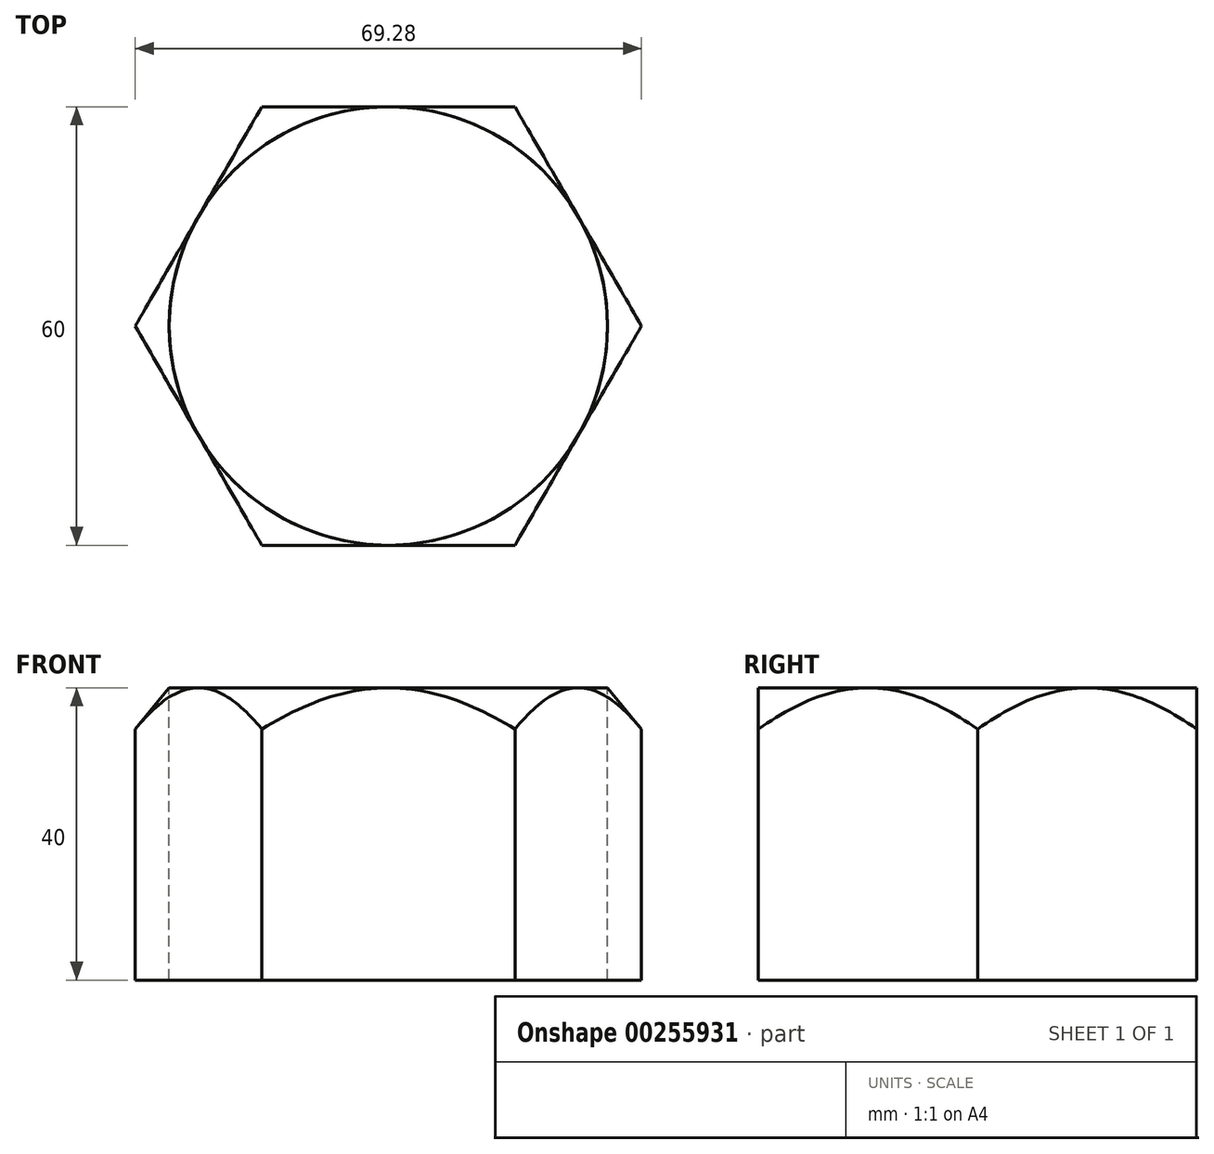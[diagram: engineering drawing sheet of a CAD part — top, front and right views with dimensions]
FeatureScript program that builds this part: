
annotation { "Feature Type Name" : "Feature", "Feature Type Description" : "" }
export const myFeature = defineFeature(function(context is Context, id is Id, definition is map)
    precondition{}
    {
        {
            var Q0;
            Q0=qCreatedBy(makeId("Top.planeOp"),FACE);
            var sketch = newSketch(context, id + "F0", { "sketchPlane" : qUnion([Q0])});
            skCircle(sketch, "E0.cCircle", {"center": v(0, 0) * mm, "radius": 30 * mm, "construction": true});
            skLineSegment(sketch, "E0.0", {"start": v(-17.32, 30) * mm, "end": v(17.32, 30) * mm});
            skLineSegment(sketch, "E0.1", {"start": v(17.32, 30) * mm, "end": v(34.64, 0) * mm});
            skLineSegment(sketch, "E0.2", {"start": v(34.64, 0) * mm, "end": v(17.32, -30) * mm});
            skLineSegment(sketch, "E0.3", {"start": v(17.32, -30) * mm, "end": v(-17.32, -30) * mm});
            skLineSegment(sketch, "E0.4", {"start": v(-17.32, -30) * mm, "end": v(-34.64, 0) * mm});
            skLineSegment(sketch, "E0.5", {"start": v(-34.64, 0) * mm, "end": v(-17.32, 30) * mm});
            skPoint(sketch, "E0.0.midPoint", {"position": v(0, 30) * mm});
            skSolve(sketch);
        }
        {
            var Q0;
            Q0=makeQuery(id+"F0.imprint","IMPRINT",FACE,{"disambiguationData":[TD([[makeQuery(id+"F0.imprint","IMPRINT",EDGE,{"derivedFrom":sQuery(id+"F0.wireOp",EDGE,"E0.0")}),-1.0]])]});
            var sketch = newSketch(context, id + "F1", { "sketchPlane" : qUnion([Q0])});
            skCircle(sketch, "E1", {"center": v(0, 0) * mm, "radius": 30 * mm});
            skSolve(sketch);
        }
        {
            var Q0;
            {var subQ0=sQuery(id+"F1.wireOp",EDGE,"E1");var subQ3=makeQuery(id+"F1.imprint","INTERSECT",VERTEX,{"derivedFrom":[makeQuery(id+"F0.imprint","IMPRINT",EDGE,{"derivedFrom":sQuery(id+"F0.wireOp",EDGE,"E0.0")}),subQ0]});Q0=makeQuery(id+"F1.imprint","IMPRINT",FACE,{"disambiguationData":[TD([[makeQuery(id+"F1.imprint","IMPRINT",EDGE,{"disambiguationData":[TD([[subQ3,1.0]])],"derivedFrom":subQ0}),1.0]])]});}
            var Q1;
            Q1=makeQuery(id+"F0.imprint","IMPRINT",FACE,{"disambiguationData":[TD([[makeQuery(id+"F0.imprint","IMPRINT",EDGE,{"derivedFrom":sQuery(id+"F0.wireOp",EDGE,"E0.0")}),-1.0]])]});
            extrude(context, id + "F2", {"entities" : qUnion([Q0, Q1]), "oppositeDirection" : true, "depth" : 40 * mm});
        }
        {
            var Q0;
            Q0=qCreatedBy(makeId("Front.planeOp"),FACE);
            var sketch = newSketch(context, id + "F3", { "sketchPlane" : qUnion([Q0])});
            skLineSegment(sketch, "E2.0", {"start": v(-30, 0) * mm, "end": v(30, 0) * mm});
            skLineSegment(sketch, "E3.0.0", {"start": v(34.64, 0) * mm, "end": v(17.32, 0) * mm});
            skLineSegment(sketch, "E3.0.1", {"start": v(17.32, 0) * mm, "end": v(17.32, -40) * mm});
            skLineSegment(sketch, "E3.0.2", {"start": v(17.32, -40) * mm, "end": v(34.64, -40) * mm});
            skLineSegment(sketch, "E3.0.3", {"start": v(34.64, -40) * mm, "end": v(34.64, 0) * mm});
            skLineSegment(sketch, "E4", {"start": v(30, 0) * mm, "end": v(34.64, -5.67) * mm});
            skLineSegment(sketch, "E5", {"start": v(0, 19.62) * mm, "end": v(0, -50.83) * mm});
            skSolve(sketch);
        }
        {
            var Q0;
            {var subQ3=sQuery(id+"F3.wireOp",EDGE,"E4");Q0=makeQuery(id+"F3.imprint","IMPRINT",FACE,{"disambiguationData":[TD([[makeQuery(id+"F3.imprint","IMPRINT",EDGE,{"derivedFrom":subQ3}),1.0]])]});}
            var Q1;
            Q1=sQuery(id+"F3.wireOp",EDGE,"E5");
            revolve(context, id + "F4", {"operationType" : NewBodyOperationType.REMOVE, "entities" : qUnion([Q0]), "axis" : qUnion([Q1]), "revolveType" : RevolveType.FULL, "oppositeDirection" : true});
        }
    });
